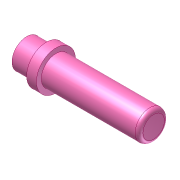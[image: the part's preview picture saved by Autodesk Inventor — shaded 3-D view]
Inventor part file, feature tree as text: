
AUTODESK INVENTOR PART (.ipt)
format: ipt  version: unknown  size: 175,616 bytes
history: native  units: mm
features: revolve x1, fillet x1, sketch x1
ambient origin geometry x8: Origin, YZ Plane, XZ Plane, XY Plane, X Axis, Y Axis, Z Axis, Center Point
feature tree (3):
  revolve  "Revolution1"  [1 undecoded]
  fillet  "Fillet1"  Radius=0.5mm
  sketch  "Sketch1"  dims[d0=0.75mm d1=1.0mm d2=0.5mm d3=1.0mm d4=0.75mm d5=5.0mm d6=90.0deg d7=0.2mm]
note: 1 required parameter value undecoded (feature->parameter linkage not recoverable at this tier; creation-order binding heuristic only, values carry confidence <= 0.55)
